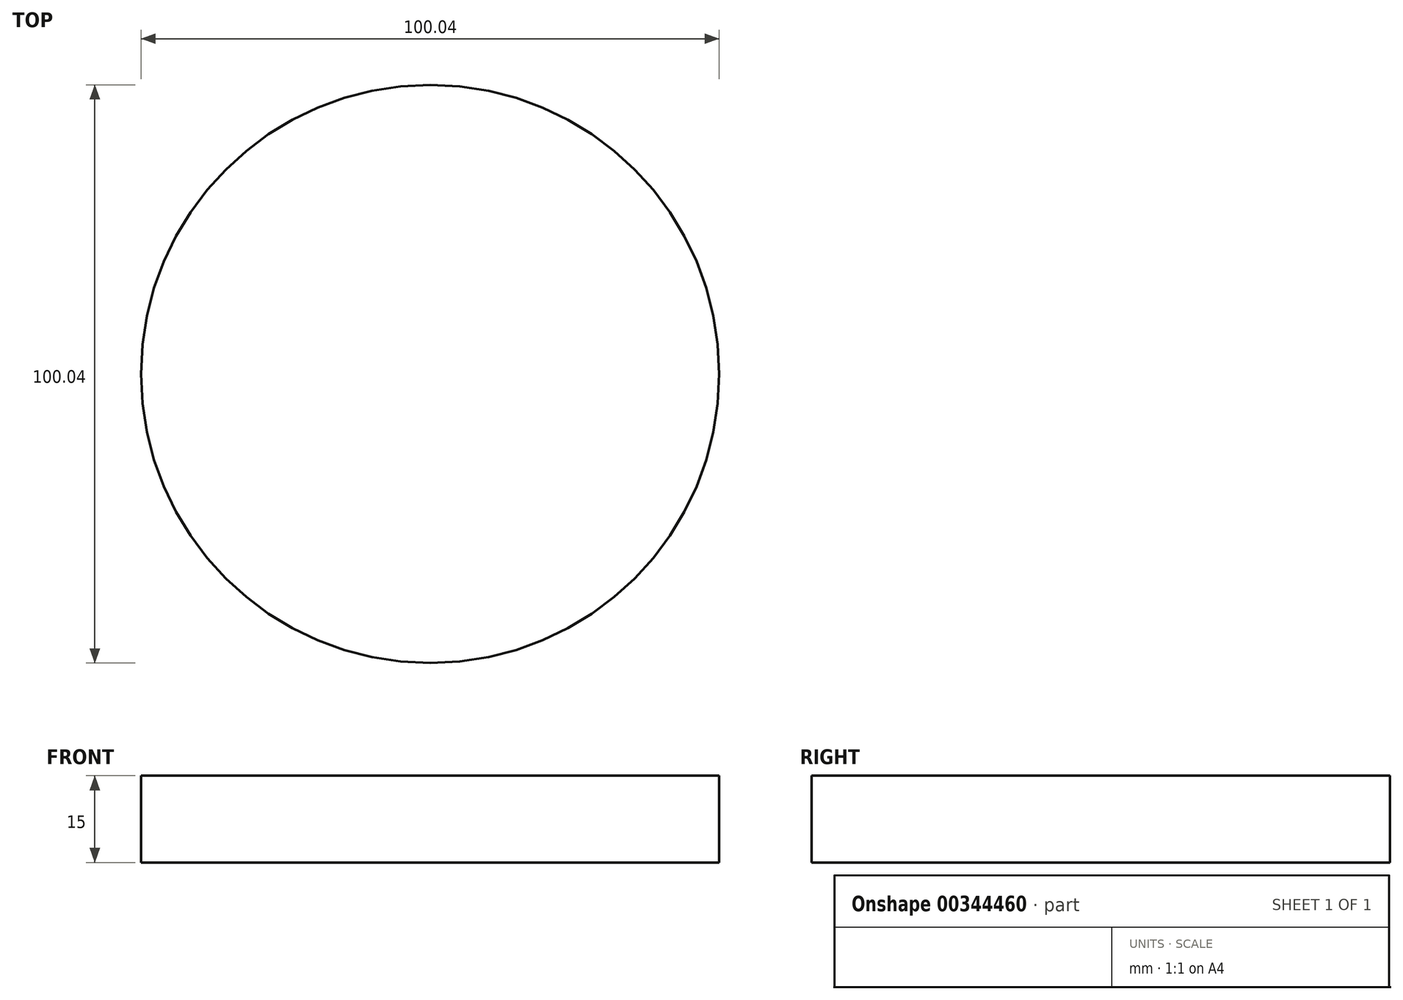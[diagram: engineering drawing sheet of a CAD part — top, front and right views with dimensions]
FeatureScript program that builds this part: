
annotation { "Feature Type Name" : "Feature", "Feature Type Description" : "" }
export const myFeature = defineFeature(function(context is Context, id is Id, definition is map)
    precondition{}
    {
        {
            var Q0;
            Q0=qCreatedBy(makeId("Top.planeOp"),FACE);
            var sketch = newSketch(context, id + "F0", { "sketchPlane" : qUnion([Q0])});
            skCircle(sketch, "E0", {"center": v(0, 0) * mm, "radius": 50.02 * mm});
            skSolve(sketch);
        }
        {
            var Q0;
            Q0 = qSketchRegion(id + "F0", true);
            extrude(context, id + "F1", {"entities" : qUnion([Q0]), "depth" : 15 * mm});
        }
    });
